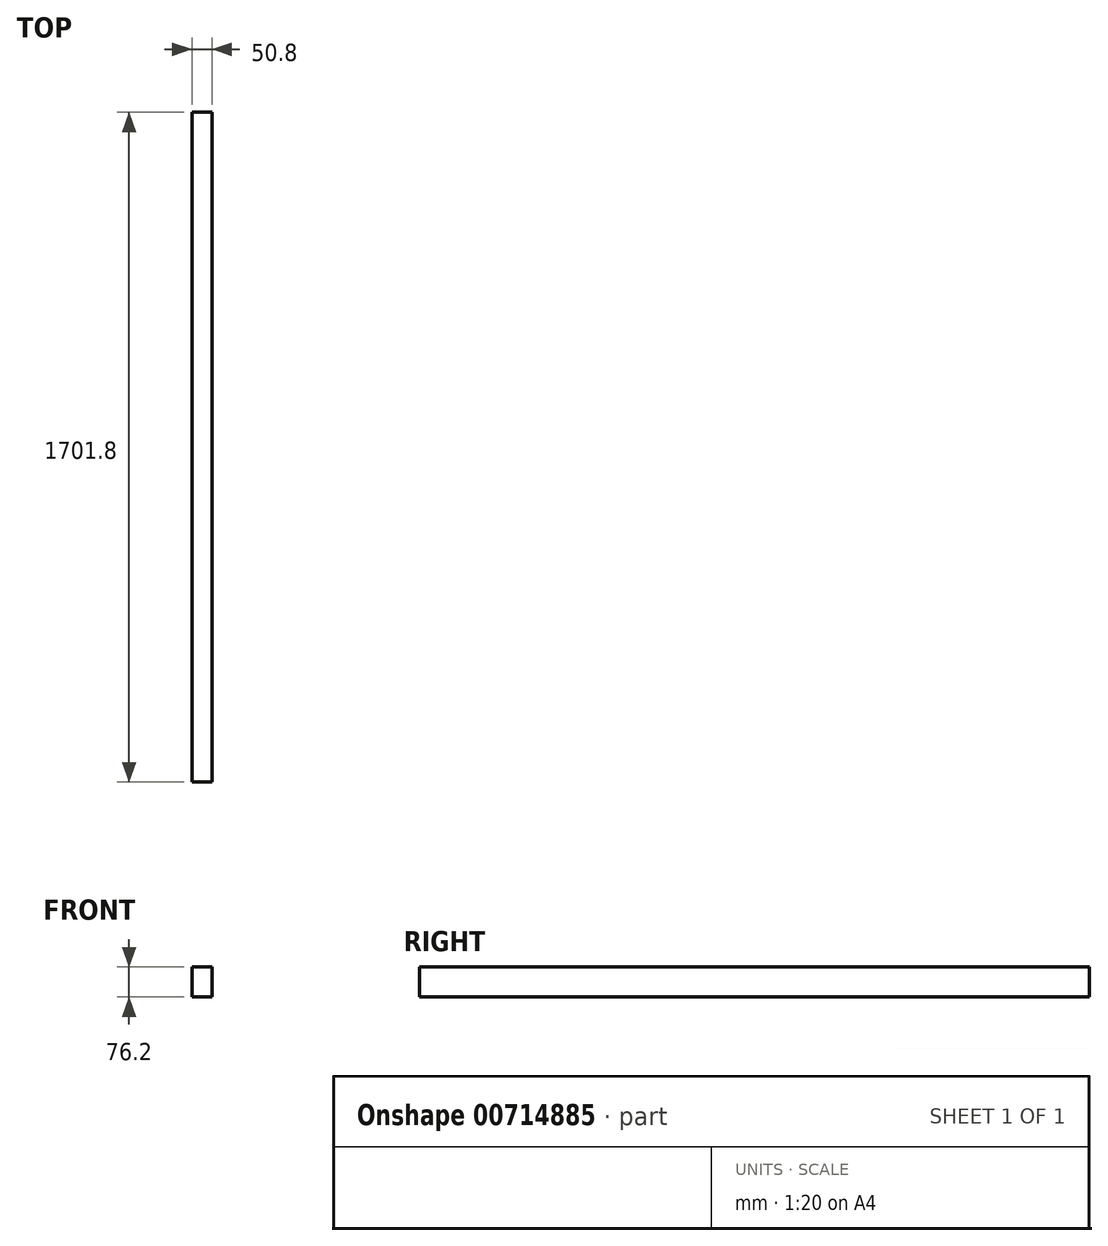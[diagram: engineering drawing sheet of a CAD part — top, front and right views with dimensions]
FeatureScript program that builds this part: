
annotation { "Feature Type Name" : "Feature", "Feature Type Description" : "" }
export const myFeature = defineFeature(function(context is Context, id is Id, definition is map)
    precondition{}
    {
        {
            var Q0;
            Q0=qCreatedBy(makeId("Right.planeOp"),FACE);
            var sketch = newSketch(context, id + "F0", { "sketchPlane" : qUnion([Q0])});
            skLineSegment(sketch, "E0.bottom", {"start": v(1701.8, 76.2) * mm, "end": v(0, 76.2) * mm});
            skLineSegment(sketch, "E0.top", {"start": v(1701.8, 0) * mm, "end": v(0, 0) * mm});
            skLineSegment(sketch, "E0.left", {"start": v(1701.8, 76.2) * mm, "end": v(1701.8, 0) * mm});
            skLineSegment(sketch, "E0.right", {"start": v(0, 76.2) * mm, "end": v(0, 0) * mm});
            skSolve(sketch);
        }
        {
            var Q0;
            Q0=makeQuery(id+"F0.imprint","IMPRINT",FACE,{"disambiguationData":[TD([[makeQuery(id+"F0.imprint","IMPRINT",EDGE,{"derivedFrom":sQuery(id+"F0.wireOp",EDGE,"E0.bottom")}),1.0]])]});
            extrude(context, id + "F1", {"entities" : qUnion([Q0]), "depth" : 50.8 * mm, "offsetDistance" : 25.4 * mm});
        }
    });
